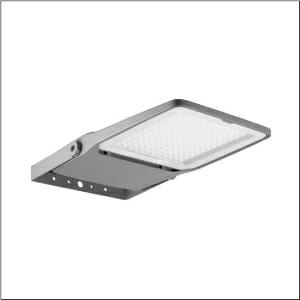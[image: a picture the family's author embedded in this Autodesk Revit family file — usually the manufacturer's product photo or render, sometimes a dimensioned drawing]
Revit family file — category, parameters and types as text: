
# Revit family: floodlight_fl_20_midi___pl43_5xa7682d1a2ac_194d
name_source: partatom
category: Lighting Fixtures
units: mm (PartAtom-declared; Revit-internal decimal feet)

## family parameters
Cut with Voids When Loaded = No
Host = Face
Light Source = No
Part Type = Normal
Room Calculation Point = No
Round Connector Dimension = Use Diameter
Shared = No

## types (1)
- --- (1 x LED 3000K / CRI = 80 (unbekannt), 14980 lm, 3000K)
    Apparent Load = 142 VA
    CIE Flux Codes = 32 74 99 100 100
    Color Rendering = 80
    Color Temperature = 3000K
    Default Elevation = 1800 mm
    Description = Floodlight FL 20 midi, floodlight, primary light control with lens, of plastic, primary optical cover: protective disc, of toughened safety glass, transparent, light distribution: PL43, light emission: direct distribution, primary light characteristic: asymmetric, installation type: surface-mounted, LED, High Power LED, rated luminous flux: 14.980lm, luminous efficacy: 105lm/W, light colour: 830, colour temperature: 3000K, control gear: ECG Plus, control: flexible luminous flux parameterisation, time-dependent luminous flux control, digital communication interface, power reduction, overheat protection, electronic power reduction, with terminal, 5-pole, max. 2.5mm², mains connection: 220..240V, AC, 50/60Hz, rated input power: 142W, LED unit, of diecast aluminium, powder-coated, Siteco® metallic grey (DB 702S), corrosivity category C5 mid according to DIN EN ISO 12944, incl. 1x M20 cable gland for cable Ø 6.5..12mm, length: 731mm, width: 450mm, height: 76mm, housing frame, of diecast aluminium, powder-coated, Siteco® metallic grey (DB 702S), wall fastening, of steel, powder-coated, Siteco® metallic grey (DB 702S), DALI, protection rating (complete): IP66, insulation class (complete): insulation class II (safety insulation), certification: CE, ENEC, VDE, protection symbol: D, permissible operating ambient temperature: -40..+40°C, permissible operating ambient temperature for outdoor applications: -40..+50°C, standard: DIN EN 12944, packaging unit: 1 piece

Light Distribution: PL43
    Height = 76 mm
    Lamp = 1 x LED 3000K / CRI >= 80 (unbekannt)
    Lamp Light Flux = 14980 lm
    Lamp count = 1
    Length = 731 mm
    Luminous efficacy = 105 lm/W
    Manufacturer = Siteco
    ModVariant = No
    Model = 5XA7682D1A2AC
    Mounting Place = Wall
    Mounting Type = Surface mounted
    Number of Poles = 1
    OnlyDefault = Yes
    Power Factor = 1
    Product Name = Floodlight FL 20 midi | PL43
    Product group = floodlight | wall mounted
    ProductGroupID = 2001
    Protection Class = Protection class II
    Protection Degree = IP 66
    RLX_Detail_Level = 1
    RLX_Emergency_Light_Flux = 0 lm
    RLX_Emergency_Type = 0
    RLX_Emergency_Type_DB = No
    RlxData = <blob elided: 91857 chars, md5=d15e7db1>
    Socket = socket
    Standby Power = 0 W
    System Light Flux = 14980 lm
    System Power = 142 W
    Type Comments = factory setting: luminous flux: 100 % | dim-lin: 254 | 489 mA
    Type Image = l_1005944.jpg
    URL = http://relux.com
    VarID = @adj_148693
    Voltage = 0 V
    Weight = 0.00 kg
    Width = 450 mm

## geometry (parser evidence)
native form markers: Blend x4, Sweep x11
no freeform markers — native parametric forms only
